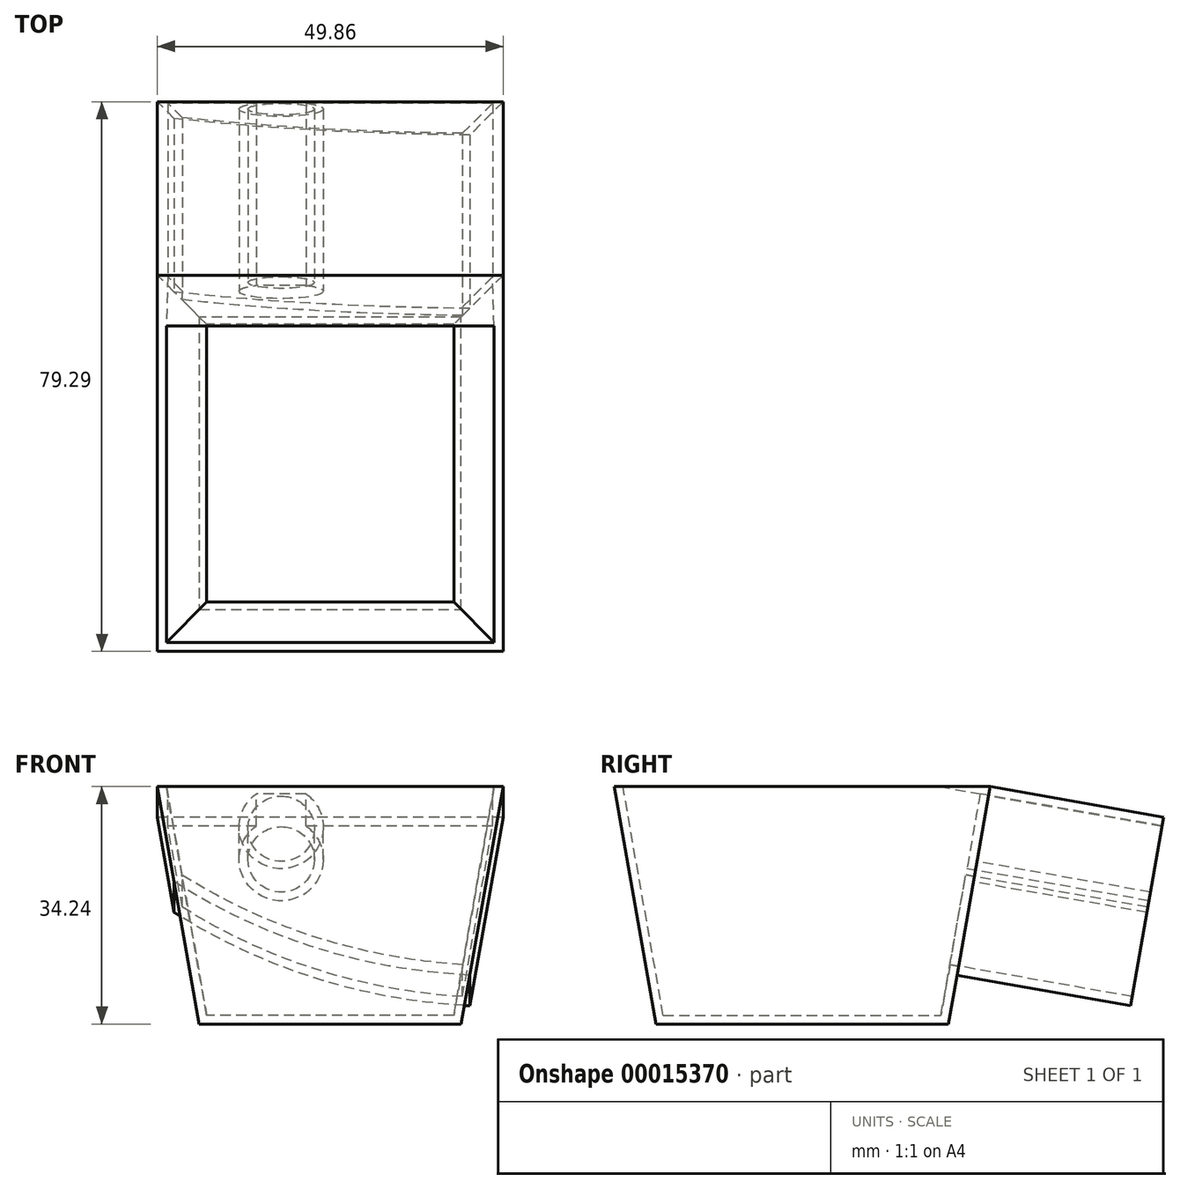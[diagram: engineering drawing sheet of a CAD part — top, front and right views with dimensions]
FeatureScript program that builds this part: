
annotation { "Feature Type Name" : "Feature", "Feature Type Description" : "" }
export const myFeature = defineFeature(function(context is Context, id is Id, definition is map)
    precondition{}
    {
        {
            var Q0;
            Q0=qCreatedBy(makeId("Top.planeOp"),FACE);
            var sketch = newSketch(context, id + "F0", { "sketchPlane" : qUnion([Q0])});
            skLineSegment(sketch, "E0.rect.bottom", {"start": v(24.93, 27.14) * mm, "end": v(-24.93, 27.14) * mm});
            skLineSegment(sketch, "E0.rect.top", {"start": v(24.93, -27.14) * mm, "end": v(-24.93, -27.14) * mm});
            skLineSegment(sketch, "E0.rect.left", {"start": v(24.93, 27.14) * mm, "end": v(24.93, -27.14) * mm});
            skLineSegment(sketch, "E0.rect.right", {"start": v(-24.93, 27.14) * mm, "end": v(-24.93, -27.14) * mm});
            skPoint(sketch, "E0.rect.middle", {"position": v(0, 0) * mm});
            skSolve(sketch);
        }
        {
            var Q0;
            Q0 = qSketchRegion(id + "F0", true);
            var Q1;
            Q1=sQuery(id+"F0.wireOp",EDGE,"E0.rect.right");
            var Q2;
            Q2=sQuery(id+"F0.wireOp",EDGE,"E0.rect.top");
            var Q3;
            Q3=sQuery(id+"F0.wireOp",EDGE,"E0.rect.left");
            var Q4;
            Q4=sQuery(id+"F0.wireOp",EDGE,"E0.rect.bottom");
            extrude(context, id + "F1", {"entities" : qUnion([Q0]), "surfaceEntities" : qUnion([Q1, Q2, Q3, Q4]), "oppositeDirection" : true, "depth" : 34.24 * mm, "hasDraft" : true, "draftAngle" : 10 * degree, "draftPullDirection" : true});
        }
        {
            var Q0;
            Q0=makeQuery(id+"F1.opExtrude","SWEPT_FACE",FACE,{"disambiguationData":[OSD([sQuery(id+"F0.wireOp",EDGE,"E0.rect.bottom")])]});
            var sketch = newSketch(context, id + "F2", { "sketchPlane" : qUnion([Q0])});
            skCircle(sketch, "E1", {"center": v(-24.06, 62.78) * mm, "radius": 85.76 * mm});
            skPoint(sketch, "E1.first.point", {"position": v(-8.3, -21.52) * mm});
            skPoint(sketch, "E1.second.point", {"position": v(10.24, -15.82) * mm});
            skPoint(sketch, "E1.third.point", {"position": v(0, -19.54) * mm});
            skCircle(sketch, "E2", {"center": v(-3.96, 0.9) * mm, "radius": 12.16 * mm});
            skPoint(sketch, "E2.first.point", {"position": v(8.17, 0) * mm});
            skPoint(sketch, "E2.second.point", {"position": v(-8.3, -10.46) * mm});
            skPoint(sketch, "E2.third.point", {"position": v(0, -10.6) * mm});
            skCircle(sketch, "E3", {"center": v(7.08, -1.47) * mm, "radius": 4.8 * mm});
            skPoint(sketch, "E3.first.point", {"position": v(2.52, 0) * mm});
            skPoint(sketch, "E3.second.point", {"position": v(2.91, 0.9) * mm});
            skPoint(sketch, "E3.third.point", {"position": v(5.96, -6.13) * mm});
            skSolve(sketch);
        }
        {
            var Q0;
            {var subQ0=sQuery(id+"F2.wireOp",EDGE,"E3");var subQ1=sQuery(id+"F2.wireOp",EDGE,"E2");var subQ3=makeQuery(id+"F2.imprint","INTERSECT",VERTEX,{"disambiguationData":[OD(0.0)],"derivedFrom":[subQ1,subQ0]});Q0=makeQuery(id+"F2.imprint","IMPRINT",FACE,{"disambiguationData":[TD([[makeQuery(id+"F2.imprint","IMPRINT",EDGE,{"disambiguationData":[TD([[subQ3,1.0]])],"derivedFrom":subQ1}),-1.0]])]});}
            var Q1;
            {var subQ0=sQuery(id+"F2.wireOp",EDGE,"E3");var subQ1=sQuery(id+"F2.wireOp",EDGE,"E2");var subQ3=makeQuery(id+"F2.imprint","INTERSECT",VERTEX,{"disambiguationData":[OD(0.0)],"derivedFrom":[subQ1,subQ0]});Q1=makeQuery(id+"F2.imprint","IMPRINT",FACE,{"disambiguationData":[TD([[makeQuery(id+"F2.imprint","IMPRINT",EDGE,{"disambiguationData":[TD([[subQ3,1.0]])],"derivedFrom":subQ1}),1.0]])]});}
            extrude(context, id + "F3", {"entities" : qUnion([Q0, Q1]), "operationType" : NewBodyOperationType.ADD, "depth" : 25.4 * mm});
        }
        {
            var Q0;
            Q0=makeQuery(id+"F1.opExtrude","CAP_FACE",FACE,{"disambiguationData":[OSD([sQuery(id+"F0.wireOp",EDGE,"E0.rect.bottom"),sQuery(id+"F0.wireOp",EDGE,"E0.rect.top"),sQuery(id+"F0.wireOp",EDGE,"E0.rect.left"),sQuery(id+"F0.wireOp",EDGE,"E0.rect.right")])],"isStart":true});
            var Q1;
            Q1=makeQuery(id+"F3.opExtrude","CAP_FACE",FACE,{"disambiguationData":[OSD([sQuery(id+"F2.wireOp",EDGE,"E3")])],"isStart":false});
            shell(context, id + "F4", {"entities" : qUnion([Q0, Q1]), "thickness" : 1.27 * mm});
        }
    });
